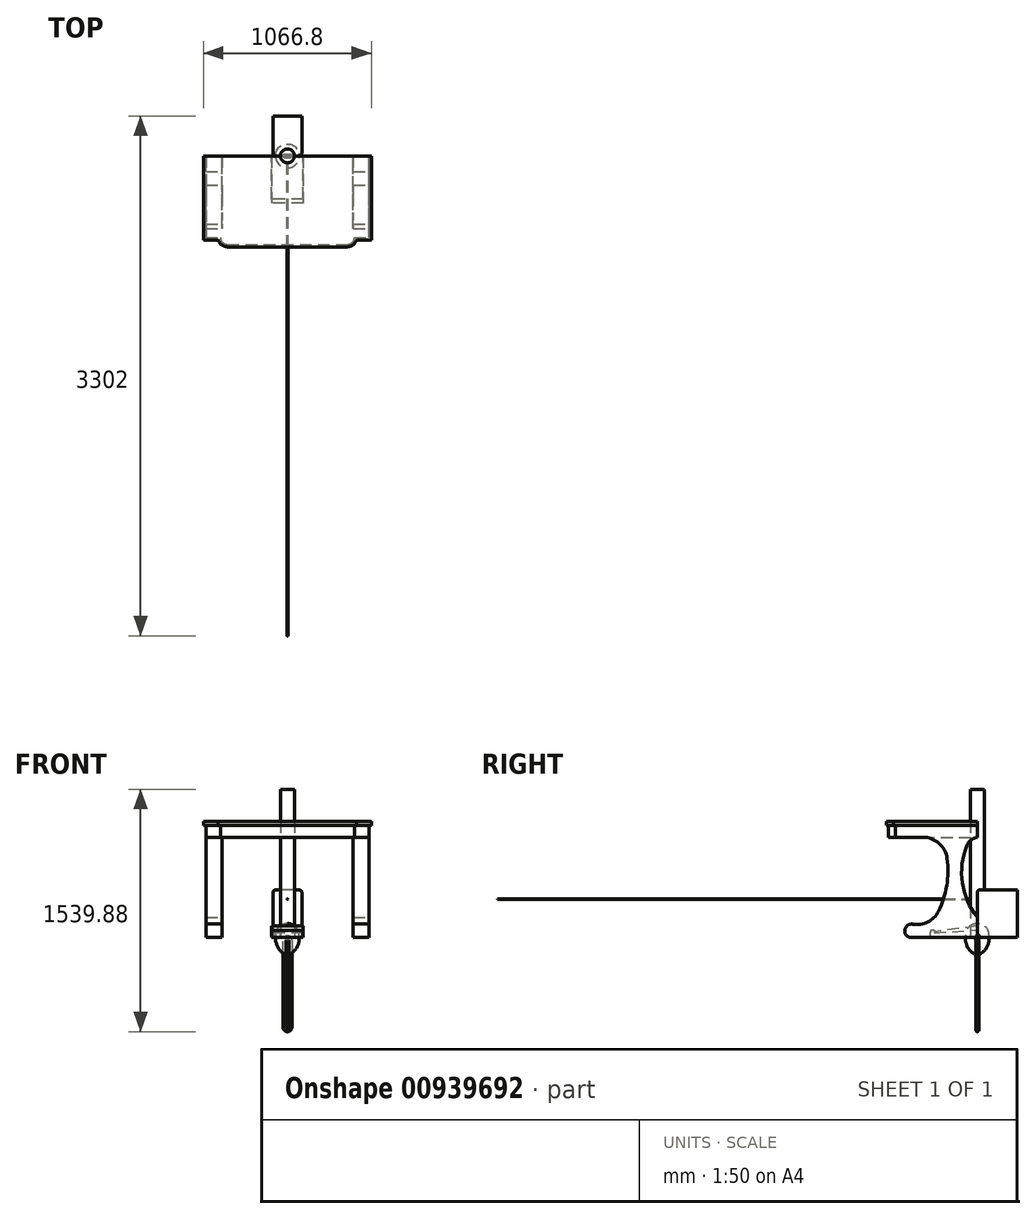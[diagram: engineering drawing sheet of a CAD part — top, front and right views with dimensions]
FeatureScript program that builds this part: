
annotation { "Feature Type Name" : "Feature", "Feature Type Description" : "" }
export const myFeature = defineFeature(function(context is Context, id is Id, definition is map)
    precondition{}
    {
        {
            var Q0;
            Q0=qCreatedBy(makeId("Top.planeOp"),FACE);
            var sketch = newSketch(context, id + "F0", { "sketchPlane" : qUnion([Q0])});
            skLineSegment(sketch, "E0", {"start": v(0, 0) * mm, "end": v(-3048, -3048) * mm});
            skLineSegment(sketch, "E1", {"start": v(0, 0) * mm, "end": v(3048, -3048) * mm});
            skLineSegment(sketch, "E2", {"start": v(-3048, -3048) * mm, "end": v(3048, -3048) * mm, "construction": true});
            skSolve(sketch);
        }
        {
            var Q0;
            Q0 = qSketchRegion(id + "F0", true);
            var Q1;
            Q1 = qConstructionFilter(qBodyType(qCreatedBy(id + "F0" ,EDGE), BodyType.WIRE), ConstructionObject.NO);
            extrude(context, id + "F1", {"entities" : qUnion([Q0]), "bodyType" : ToolBodyType.SURFACE, "surfaceEntities" : qUnion([Q1]), "depth" : 3048 * mm, "offsetDistance" : 25.4 * mm});
        }
        {
            var Q0;
            Q0=makeQuery(id+"F1.opExtrude","SWEPT_FACE",FACE,{"disambiguationData":[OSD([sQuery(id+"F0.wireOp",EDGE,"E0")])]});
            var sketch = newSketch(context, id + "F2", { "sketchPlane" : qUnion([Q0])});
            skLineSegment(sketch, "E3", {"start": v(0, 0) * mm, "end": v(4310.52, 0) * mm});
            skSolve(sketch);
        }
        {
            var Q0;
            Q0 = qSketchRegion(id + "F2", true);
            var Q1;
            Q1 = qConstructionFilter(qBodyType(qCreatedBy(id + "F2" ,EDGE), BodyType.WIRE), ConstructionObject.NO);
            var Q2;
            Q2=makeQuery(id+"F1.opExtrude","CAP_VERTEX",VERTEX,{"disambiguationData":[OSD([sQuery(id+"F0.wireOp",VERTEX,"E1.end")])],"isStart":true});
            extrude(context, id + "F3", {"entities" : qUnion([Q0]), "bodyType" : ToolBodyType.SURFACE, "surfaceEntities" : qUnion([Q1]), "endBound" : BoundingType.UP_TO_VERTEX, "oppositeDirection" : true, "depth" : 3048 * mm, "endBoundEntityVertex" : qUnion([Q2]), "offsetDistance" : 25.4 * mm});
        }
        {
            var Q0;
            Q0=qCreatedBy(makeId("Top.planeOp"),FACE);
            var sketch = newSketch(context, id + "F4", { "sketchPlane" : qUnion([Q0])});
            skLineSegment(sketch, "E4", {"start": v(-533.4, -533.4) * mm, "end": v(-533.4, 0) * mm});
            skLineSegment(sketch, "E5", {"start": v(-533.4, 0) * mm, "end": v(533.4, 0) * mm});
            skLineSegment(sketch, "E6", {"start": v(533.4, 0) * mm, "end": v(533.4, -533.4) * mm});
            skLineSegment(sketch, "E7", {"start": v(-533.4, -533.4) * mm, "end": v(-438.93, -533.4) * mm});
            skArc(sketch, "E8", {"start": v(-438.93, -533.4) * mm, "mid": v(-417.5, -565.46) * mm, "end": v(-381, -577.85) * mm});
            skLineSegment(sketch, "E9", {"start": v(-381, -577.85) * mm, "end": v(381, -577.85) * mm});
            skArc(sketch, "E10", {"start": v(381, -577.85) * mm, "mid": v(417.5, -565.46) * mm, "end": v(438.93, -533.4) * mm});
            skLineSegment(sketch, "E11", {"start": v(533.4, -533.4) * mm, "end": v(438.93, -533.4) * mm});
            skLineSegment(sketch, "E12", {"start": v(-438.93, -533.4) * mm, "end": v(-533.4, -180.83) * mm, "construction": true});
            skSolve(sketch);
        }
        {
            var Q0;
            Q0 = qSketchRegion(id + "F4", true);
            extrude(context, id + "F5", {"entities" : qUnion([Q0]), "depth" : 736.6 * mm, "offsetDistance" : 25.4 * mm, "hasSecondDirection" : true, "secondDirectionOppositeDirection" : false, "secondDirectionDepth" : 711.2 * mm});
        }
        {
            var Q0;
            Q0=makeQuery(id+"F5.opExtrude","CAP_FACE",FACE,{"disambiguationData":[OSD([sQuery(id+"F4.wireOp",EDGE,"E4"),sQuery(id+"F4.wireOp",EDGE,"E5"),sQuery(id+"F4.wireOp",EDGE,"E6"),sQuery(id+"F4.wireOp",EDGE,"E7"),sQuery(id+"F4.wireOp",EDGE,"E8"),sQuery(id+"F4.wireOp",EDGE,"E9"),sQuery(id+"F4.wireOp",EDGE,"E10"),sQuery(id+"F4.wireOp",EDGE,"E11")])],"isStart":true});
            var sketch = newSketch(context, id + "F6", { "sketchPlane" : qUnion([Q0])});
            skLineSegment(sketch, "E13", {"start": v(-518.16, 0) * mm, "end": v(-518.16, 518.16) * mm});
            skLineSegment(sketch, "E14", {"start": v(-518.16, 518.16) * mm, "end": v(-425.73, 518.16) * mm});
            skArc(sketch, "E15", {"start": v(-381, 562.61) * mm, "mid": v(-412.53, 549.6) * mm, "end": v(-425.73, 518.16) * mm});
            skLineSegment(sketch, "E16", {"start": v(-381, 562.6) * mm, "end": v(381, 562.6) * mm});
            skArc(sketch, "E17", {"start": v(425.73, 518.16) * mm, "mid": v(412.53, 549.6) * mm, "end": v(381, 562.6) * mm});
            skLineSegment(sketch, "E18", {"start": v(425.73, 518.16) * mm, "end": v(518.16, 518.16) * mm});
            skLineSegment(sketch, "E19", {"start": v(518.16, 518.16) * mm, "end": v(518.16, 0) * mm});
            skLineSegment(sketch, "E20", {"start": v(518.16, 0) * mm, "end": v(-518.16, 0) * mm});
            skLineSegment(sketch, "E21", {"start": v(-518.16, 518.16) * mm, "end": v(-518.16, 533.4) * mm, "construction": true});
            skLineSegment(sketch, "E22", {"start": v(-518.16, 518.16) * mm, "end": v(-533.4, 518.16) * mm, "construction": true});
            skLineSegment(sketch, "E23", {"start": v(-381, 562.6) * mm, "end": v(-381, 577.85) * mm, "construction": true});
            skSolve(sketch);
        }
        {
            var Q0;
            Q0 = qSketchRegion(id + "F6", true);
            var Q1;
            Q1=qCreatedBy(makeId("Origin.pointOp"),VERTEX);
            extrude(context, id + "F7", {"entities" : qUnion([Q0]), "operationType" : NewBodyOperationType.ADD, "endBound" : BoundingType.UP_TO_VERTEX, "depth" : 25.4 * mm, "endBoundEntityVertex" : qUnion([Q1]), "offsetDistance" : 25.4 * mm});
        }
        {
            var Q0;
            Q0=qCreatedBy(makeId("Right.planeOp"),FACE);
            var sketch = newSketch(context, id + "F8", { "sketchPlane" : qUnion([Q0])});
            skLineSegment(sketch, "E24", {"start": v(-562.6, 635) * mm, "end": v(-345.94, 635) * mm});
            skLineSegment(sketch, "E25", {"start": v(-562.6, 635) * mm, "end": v(-562.6, 0) * mm});
            skLineSegment(sketch, "E26", {"start": v(-562.6, 0) * mm, "end": v(-434.38, 0) * mm});
            skArc(sketch, "E27", {"start": v(-190.99, 498.93) * mm, "mid": v(-242.83, 596.15) * mm, "end": v(-345.94, 635) * mm});
            skArc(sketch, "E28", {"start": v(0, 635) * mm, "mid": v(-39.83, 616.81) * mm, "end": v(-65.84, 581.6) * mm});
            skArc(sketch, "E29", {"start": v(-65.84, 581.6) * mm, "mid": v(-94.28, 345.05) * mm, "end": v(0, 126.25) * mm});
            skArc(sketch, "E30", {"start": v(-245.7, 164.55) * mm, "mid": v(-193.78, 327.72) * mm, "end": v(-190.99, 498.93) * mm});
            skArc(sketch, "E31", {"start": v(-409.23, 82.4) * mm, "mid": v(-313.6, 95.87) * mm, "end": v(-245.7, 164.55) * mm});
            skArc(sketch, "E32", {"start": v(-409.23, 82.4) * mm, "mid": v(-458.7, 52.46) * mm, "end": v(-434.38, 0) * mm});
            skLineSegment(sketch, "E33", {"start": v(0, 635) * mm, "end": v(0, 126.25) * mm});
            skSolve(sketch);
        }
        {
            var Q0;
            Q0 = qSketchRegion(id + "F8", true);
            extrude(context, id + "F9", {"entities" : qUnion([Q0]), "operationType" : NewBodyOperationType.REMOVE, "endBound" : BoundingType.THROUGH_ALL, "oppositeDirection" : true, "depth" : 25.4 * mm, "offsetDistance" : 25.4 * mm, "hasSecondDirection" : true, "secondDirectionBound" : SecondDirectionBoundingType.THROUGH_ALL, "secondDirectionOppositeDirection" : false, "secondDirectionDepth" : 25.4 * mm});
        }
        {
            var Q0;
            Q0=qCreatedBy(makeId("Front.planeOp"),FACE);
            var sketch = newSketch(context, id + "F10", { "sketchPlane" : qUnion([Q0])});
            skLineSegment(sketch, "E34.bottom", {"start": v(-416.56, 0) * mm, "end": v(416.56, 0) * mm});
            skLineSegment(sketch, "E34.top", {"start": v(-416.56, 635) * mm, "end": v(416.56, 635) * mm});
            skLineSegment(sketch, "E34.left", {"start": v(-416.56, 0) * mm, "end": v(-416.56, 635) * mm});
            skLineSegment(sketch, "E34.right", {"start": v(416.56, 0) * mm, "end": v(416.56, 635) * mm});
            skSolve(sketch);
        }
        {
            var Q0;
            Q0 = qSketchRegion(id + "F10", true);
            extrude(context, id + "F11", {"entities" : qUnion([Q0]), "operationType" : NewBodyOperationType.REMOVE, "endBound" : BoundingType.THROUGH_ALL, "depth" : 25.4 * mm, "offsetDistance" : 25.4 * mm});
        }
        {
            var Q0;
            Q0=qCreatedBy(makeId("Front.planeOp"),FACE);
            var sketch = newSketch(context, id + "F12", { "sketchPlane" : qUnion([Q0])});
            skFitSpline(sketch, "E35", {"points": [v(0, 87.22) * mm, v(-56.27, 62.75) * mm, v(-57.44, -69.47) * mm, v(0, -115.98) * mm], "startDerivative": vector(-80.35, 0) * mm, "endDerivative": vector(61.54, 0) * mm});
            skLineSegment(sketch, "E36", {"start": v(0, 87.22) * mm, "end": v(76.2, 87.22) * mm, "construction": true});
            skLineSegment(sketch, "E37", {"start": v(0, -115.98) * mm, "end": v(76.2, -115.98) * mm, "construction": true});
            skLineSegment(sketch, "E38", {"start": v(0, 87.22) * mm, "end": v(0, -115.98) * mm, "construction": true});
            skLineSegment(sketch, "E39", {"start": v(-76.2, 87.22) * mm, "end": v(-76.2, -115.98) * mm, "construction": true});
            skPoint(sketch, "E40", {"position": v(-76.2, 0) * mm});
            skLineSegment(sketch, "E41", {"start": v(0, 87.22) * mm, "end": v(0, -115.98) * mm});
            skSolve(sketch);
        }
        {
            var Q0;
            Q0 = qSketchRegion(id + "F12", true);
            var Q1;
            Q1=sQuery(id+"F12.wireOp",EDGE,"E41");
            revolve(context, id + "F13", {"surfaceOperationType" : NewSurfaceOperationType.NEW, "entities" : qUnion([Q0]), "axis" : qUnion([Q1]), "revolveType" : RevolveType.FULL});
        }
        {
            var Q0;
            Q0=qCreatedBy(makeId("Front.planeOp"),FACE);
            var sketch = newSketch(context, id + "F14", { "sketchPlane" : qUnion([Q0])});
            skLineSegment(sketch, "E42.bottom", {"start": v(-74.93, 115.98) * mm, "end": v(74.93, 115.98) * mm});
            skLineSegment(sketch, "E42.top", {"start": v(-74.93, -115.98) * mm, "end": v(74.93, -115.98) * mm});
            skLineSegment(sketch, "E42.left", {"start": v(-74.93, 115.98) * mm, "end": v(-74.93, -115.98) * mm});
            skLineSegment(sketch, "E42.right", {"start": v(74.93, 115.98) * mm, "end": v(74.93, -115.98) * mm});
            skPoint(sketch, "E42.middle", {"position": v(0, 0) * mm});
            skLineSegment(sketch, "E43.0", {"start": v(-100.33, 141.38) * mm, "end": v(100.33, 141.38) * mm});
            skLineSegment(sketch, "E43.1", {"start": v(-100.33, 141.38) * mm, "end": v(-100.33, -141.38) * mm});
            skLineSegment(sketch, "E43.2", {"start": v(-100.33, -141.38) * mm, "end": v(100.33, -141.38) * mm});
            skLineSegment(sketch, "E43.3", {"start": v(100.33, 141.38) * mm, "end": v(100.33, -141.38) * mm});
            skSolve(sketch);
        }
        {
            var Q0;
            Q0 = qSketchRegion(id + "F14", true);
            extrude(context, id + "F15", {"entities" : qUnion([Q0]), "operationType" : NewBodyOperationType.REMOVE, "endBound" : BoundingType.SYMMETRIC, "oppositeDirection" : true, "depth" : 152.4 * mm, "offsetDistance" : 25.4 * mm});
        }
        {
            var Q0;
            Q0=qCreatedBy(makeId("Top.planeOp"),FACE);
            var sketch = newSketch(context, id + "F16", { "sketchPlane" : qUnion([Q0])});
            skLineSegment(sketch, "E44.bottom", {"start": v(92.08, 0) * mm, "end": v(-92.08, 0) * mm});
            skLineSegment(sketch, "E44.top", {"start": v(92.08, 254) * mm, "end": v(-92.08, 254) * mm});
            skLineSegment(sketch, "E44.left", {"start": v(92.08, 0) * mm, "end": v(92.08, 254) * mm});
            skLineSegment(sketch, "E44.right", {"start": v(-92.08, 0) * mm, "end": v(-92.08, 254) * mm});
            skPoint(sketch, "E44.middle", {"position": v(0, 127) * mm});
            skCircle(sketch, "E45", {"center": v(0, 127) * mm, "radius": 156.87 * mm, "construction": true});
            skSolve(sketch);
        }
        {
            var Q0;
            Q0=makeQuery(id+"F16.imprint","IMPRINT",FACE,{"disambiguationData":[TD([[makeQuery(id+"F16.imprint","IMPRINT",EDGE,{"derivedFrom":sQuery(id+"F16.wireOp",EDGE,"E44.bottom")}),-1.0]])]});
            extrude(context, id + "F17", {"entities" : qUnion([Q0]), "depth" : 301.62 * mm, "offsetDistance" : 25.4 * mm});
        }
        {
            var Q0;
            Q0=qCreatedBy(makeId("Right.planeOp"),FACE);
            var sketch = newSketch(context, id + "F18", { "sketchPlane" : qUnion([Q0])});
            skArc(sketch, "E46", {"start": v(0, 241.3) * mm, "mid": v(0.97, 234.67) * mm, "end": v(3.8, 228.6) * mm});
            skArc(sketch, "E47", {"start": v(0.68, 223.18) * mm, "mid": v(0.17, 221.95) * mm, "end": v(0, 220.64) * mm});
            skLineSegment(sketch, "E48", {"start": v(0.68, 223.18) * mm, "end": v(3.8, 228.6) * mm});
            skLineSegment(sketch, "E49", {"start": v(0, 241.3) * mm, "end": v(23.07, 241.3) * mm, "construction": true});
            skLineSegment(sketch, "E50", {"start": v(0, 241.3) * mm, "end": v(-2.54, 241.3) * mm});
            skLineSegment(sketch, "E51", {"start": v(-2.54, 241.3) * mm, "end": v(-2.54, 220.64) * mm});
            skLineSegment(sketch, "E52", {"start": v(-2.54, 220.64) * mm, "end": v(0, 220.64) * mm});
            skSolve(sketch);
        }
        {
            var Q0;
            Q0 = qSketchRegion(id + "F18", true);
            var Q1;
            Q1=sQuery(id+"F18.wireOp",EDGE,"E49");
            revolve(context, id + "F19", {"operationType" : NewBodyOperationType.REMOVE, "surfaceOperationType" : NewSurfaceOperationType.NEW, "entities" : qUnion([Q0]), "axis" : qUnion([Q1]), "revolveType" : RevolveType.FULL, "oppositeDirection" : true});
        }
        {
            var Q0;
            Q0=makeQuery(id+"F17.opExtrude","CAP_EDGE",EDGE,{"disambiguationData":[OSD([sQuery(id+"F16.wireOp",EDGE,"E44.left")])],"isStart":false});
            var Q1;
            Q1=makeQuery(id+"F17.opExtrude","CAP_EDGE",EDGE,{"disambiguationData":[OSD([sQuery(id+"F16.wireOp",EDGE,"E44.right")])],"isStart":false});
            var Q2;
            Q2=makeQuery(id+"F17.opExtrude","CAP_EDGE",EDGE,{"disambiguationData":[OSD([sQuery(id+"F16.wireOp",EDGE,"E44.right")])],"isStart":true});
            var Q3;
            Q3=makeQuery(id+"F17.opExtrude","CAP_EDGE",EDGE,{"disambiguationData":[OSD([sQuery(id+"F16.wireOp",EDGE,"E44.left")])],"isStart":true});
            var Q4;
            Q4=makeQuery(id+"F17.opExtrude","CAP_EDGE",EDGE,{"disambiguationData":[OSD([sQuery(id+"F16.wireOp",EDGE,"E44.bottom")])],"isStart":true});
            var Q5;
            Q5=makeQuery(id+"F17.opExtrude","SWEPT_EDGE",EDGE,{"disambiguationData":[OSD([sQuery(id+"F16.wireOp",EDGE,"E44.bottom"),sQuery(id+"F16.wireOp",EDGE,"E44.left")])]});
            var Q6;
            Q6=makeQuery(id+"F17.opExtrude","SWEPT_EDGE",EDGE,{"disambiguationData":[OSD([sQuery(id+"F16.wireOp",EDGE,"E44.bottom"),sQuery(id+"F16.wireOp",EDGE,"E44.right")])]});
            var Q7;
            Q7=makeQuery(id+"F17.opExtrude","CAP_EDGE",EDGE,{"disambiguationData":[OSD([sQuery(id+"F16.wireOp",EDGE,"E44.bottom")])],"isStart":false});
            fillet(context, id + "F20", {"entities" : qUnion([Q0, Q1, Q2, Q3, Q4, Q5, Q6, Q7]), "radius" : 20.32 * mm, "tangentPropagation" : true, "allowEdgeOverflow" : false});
        }
        {
            var Q0;
            Q0=makeQuery(id+"F17.opExtrude","SWEPT_FACE",FACE,{"disambiguationData":[OSD([sQuery(id+"F16.wireOp",EDGE,"E44.bottom")])]});
            var sketch = newSketch(context, id + "F21", { "sketchPlane" : qUnion([Q0])});
            skCircle(sketch, "E53", {"center": v(0, 241.3) * mm, "radius": 2.54 * mm});
            skSolve(sketch);
        }
        {
            var Q0;
            Q0=qCreatedBy(makeId("Right.planeOp"),FACE);
            var sketch = newSketch(context, id + "F22", { "sketchPlane" : qUnion([Q0])});
            skLineSegment(sketch, "E54", {"start": v(0, 46.04) * mm, "end": v(0, 0) * mm});
            skLineSegment(sketch, "E55", {"start": v(0, 0) * mm, "end": v(-298.45, 0) * mm});
            skLineSegment(sketch, "E56", {"start": v(-298.45, 0) * mm, "end": v(-298.45, 31.75) * mm});
            skLineSegment(sketch, "E57", {"start": v(-273.05, 44.45) * mm, "end": v(-273.05, 26.99) * mm});
            skLineSegment(sketch, "E58", {"start": v(-273.05, 26.99) * mm, "end": v(0, 46.04) * mm});
            skLineSegment(sketch, "E59", {"start": v(-273.05, 44.45) * mm, "end": v(-285.75, 44.45) * mm});
            skPoint(sketch, "E60.visualSharp", {"position": v(-298.45, 44.45) * mm});
            skArc(sketch, "E60.filletArc", {"start": v(-285.75, 44.45) * mm, "mid": v(-294.73, 40.73) * mm, "end": v(-298.45, 31.75) * mm});
            skSolve(sketch);
        }
        {
            var Q0;
            Q0 = qSketchRegion(id + "F22", true);
            extrude(context, id + "F23", {"entities" : qUnion([Q0]), "endBound" : BoundingType.SYMMETRIC, "depth" : 200.02 * mm, "offsetDistance" : 25.4 * mm});
        }
        {
            var Q0;
            Q0=qCreatedBy(makeId("Right.planeOp"),FACE);
            var sketch = newSketch(context, id + "F24", { "sketchPlane" : qUnion([Q0])});
            skLineSegment(sketch, "E61", {"start": v(0, 46.04) * mm, "end": v(0, 0) * mm});
            skLineSegment(sketch, "E62", {"start": v(0, 0) * mm, "end": v(-298.45, 0) * mm});
            skLineSegment(sketch, "E63", {"start": v(-298.45, 0) * mm, "end": v(-298.45, 31.75) * mm});
            skLineSegment(sketch, "E64", {"start": v(-273.05, 44.45) * mm, "end": v(-273.05, 26.99) * mm, "construction": true});
            skLineSegment(sketch, "E65", {"start": v(-273.05, 26.99) * mm, "end": v(0, 46.04) * mm, "construction": true});
            skLineSegment(sketch, "E66", {"start": v(-273.05, 44.45) * mm, "end": v(-285.75, 44.45) * mm});
            skPoint(sketch, "E67.visualSharp", {"position": v(-298.45, 44.45) * mm});
            skArc(sketch, "E67.filletArc", {"start": v(-285.75, 44.45) * mm, "mid": v(-294.73, 40.73) * mm, "end": v(-298.45, 31.75) * mm});
            skLineSegment(sketch, "E68", {"start": v(-0.22, 46.02) * mm, "end": v(-1.93, 70.57) * mm});
            skLineSegment(sketch, "E69", {"start": v(-1.93, 70.57) * mm, "end": v(-273.05, 33.35) * mm});
            skLineSegment(sketch, "E70", {"start": v(-273.05, 33.35) * mm, "end": v(-272.6, 27.02) * mm, "construction": true});
            skLineSegment(sketch, "E71", {"start": v(-273.05, 44.45) * mm, "end": v(-273.05, 33.35) * mm});
            skLineSegment(sketch, "E72", {"start": v(0, 46.04) * mm, "end": v(-0.22, 46.02) * mm});
            skSolve(sketch);
        }
        {
            var Q0;
            Q0 = qSketchRegion(id + "F24", true);
            extrude(context, id + "F25", {"entities" : qUnion([Q0]), "endBound" : BoundingType.SYMMETRIC, "depth" : 200.02 * mm, "offsetDistance" : 25.4 * mm});
        }
        {
            var Q0;
            Q0=qCreatedBy(makeId("Top.planeOp"),FACE);
            var sketch = newSketch(context, id + "F26", { "sketchPlane" : qUnion([Q0])});
            skCircle(sketch, "E73", {"center": v(0, 0) * mm, "radius": 44.45 * mm});
            skSolve(sketch);
        }
        {
            var Q0;
            Q0=makeQuery(id+"F26.imprint","IMPRINT",FACE,{"disambiguationData":[TD([[makeQuery(id+"F26.imprint","IMPRINT",EDGE,{"derivedFrom":sQuery(id+"F26.wireOp",EDGE,"E73")}),1.0]])]});
            extrude(context, id + "F27", {"entities" : qUnion([Q0]), "depth" : 939.8 * mm, "offsetDistance" : 25.4 * mm});
        }
        {
            var Q0;
            Q0=qCreatedBy(makeId("Right.planeOp"),FACE);
            var sketch = newSketch(context, id + "F28", { "sketchPlane" : qUnion([Q0])});
            skCircle(sketch, "E74", {"center": v(0, 0) * mm, "radius": 9.53 * mm});
            skSolve(sketch);
        }
        {
            var Q0;
            Q0=qCreatedBy(makeId("Front.planeOp"),FACE);
            var sketch = newSketch(context, id + "F29", { "sketchPlane" : qUnion([Q0])});
            skArc(sketch, "E75", {"start": v(19.05, -19.05) * mm, "mid": v(0, 0) * mm, "end": v(-19.05, -19.05) * mm});
            skLineSegment(sketch, "E76", {"start": v(-19.05, -19.05) * mm, "end": v(-19.05, -571.5) * mm});
            skLineSegment(sketch, "E77", {"start": v(19.05, -19.05) * mm, "end": v(19.05, -571.5) * mm});
            skArc(sketch, "E78", {"start": v(-19.05, -571.5) * mm, "mid": v(0, -590.55) * mm, "end": v(19.05, -571.5) * mm});
            skSolve(sketch);
        }
        {
            var Q0;
            Q0 = qSketchRegion(id + "F28", true);
            var Q1;
            Q1 = qConstructionFilter(qBodyType(qCreatedBy(id + "F29" ,EDGE), BodyType.WIRE), ConstructionObject.NO);
            sweep(context, id + "F30", {"profiles" : qUnion([Q0]), "path" : qUnion([Q1])});
        }
        {
            var Q0;
            Q0 = qSketchRegion(id + "F21", true);
            extrude(context, id + "F31", {"entities" : qUnion([Q0]), "operationType" : NewBodyOperationType.ADD, "depth" : 3048 * mm, "offsetDistance" : 25.4 * mm, "hasSecondDirection" : true, "secondDirectionOppositeDirection" : true, "secondDirectionDepth" : 25.4 * mm});
        }
        {
            var Q0;
            Q0=qCreatedBy(makeId("Front.planeOp"),FACE);
            var sketch = newSketch(context, id + "F32", { "sketchPlane" : qUnion([Q0])});
            skLineSegment(sketch, "E79", {"start": v(0, 0) * mm, "end": v(1219.2, 0) * mm});
            skSolve(sketch);
        }
        {
            var Q0;
            Q0 = qSketchRegion(id + "F32", true);
            var Q1;
            Q1 = qConstructionFilter(qBodyType(qCreatedBy(id + "F32" ,EDGE), BodyType.WIRE), ConstructionObject.NO);
            extrude(context, id + "F33", {"entities" : qUnion([Q0]), "bodyType" : ToolBodyType.SURFACE, "surfaceEntities" : qUnion([Q1]), "oppositeDirection" : true, "depth" : 2438.4 * mm, "offsetDistance" : 25.4 * mm});
        }
    });
